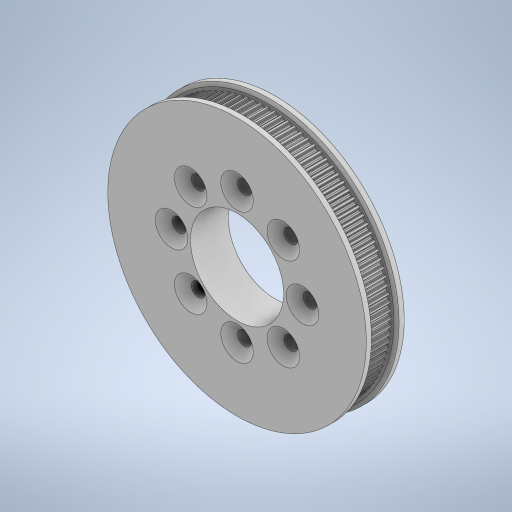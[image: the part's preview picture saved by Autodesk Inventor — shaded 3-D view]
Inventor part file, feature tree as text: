
AUTODESK INVENTOR PART (.ipt)
format: ipt  version: 2024 (Build 280153000, 153)  size: 3,681,792 bytes
history: native  units: mm
features: extrude x4, sketch x3, chamfer x2, projected_geometry x2, pattern_circular x1, mirror x1
ambient origin geometry x8: Origin, YZ Plane, XZ Plane, XY Plane, X Axis, Y Axis, Z Axis, Center Point
bodies: Solid1 (feature_tree)
feature tree (13):
  extrude  "Extrusion1"  Depth=0.277778mm
  pattern_circular  "Circular Pattern1"  [2 undecoded]
  extrude  "Extrusion2"  Depth=0.555mm
  chamfer  "Chamfer1"  Distance=1.0mm
  mirror  "Mirror1"
  extrude  "Extrusion5"  Depth=0.15mm
  extrude  "Extrusion6"  Depth=0.6mm
  chamfer  "Chamfer2"  Distance=7.0mm
  sketch  "Sketch1"  dims[d0=72.0mm d1=0.277778mm]
  sketch  "Sketch6"  dims[d2=0.111111mm]
  projected_geometry  "Projected Loop2"
  sketch  "Sketch7"  dims[d3=1.004mm d4=0.75mm d5=0.555mm d6=1.0mm d7=0.15mm d9=0.6mm d10=7.0mm d11=0.0mm d12=1130.973355mm d13=360.0deg d15=75.0mm d16=2.0mm d17=0.0mm d18=1.0mm d19=0.5mm d20=45.0deg d21=5.0mm d31=27.0mm d32=0.0mm d33=0.0mm d34=19.0mm d35=4.0mm d36=80.0mm d38=360.0deg d40=0.0mm d41=0.0mm d42=2.7mm d43=2.2mm d44=45.0deg]
  projected_geometry  "Projected Loop3"
note: 2 required parameter values undecoded (feature->parameter linkage not recoverable at this tier; creation-order binding heuristic only, values carry confidence <= 0.55)
